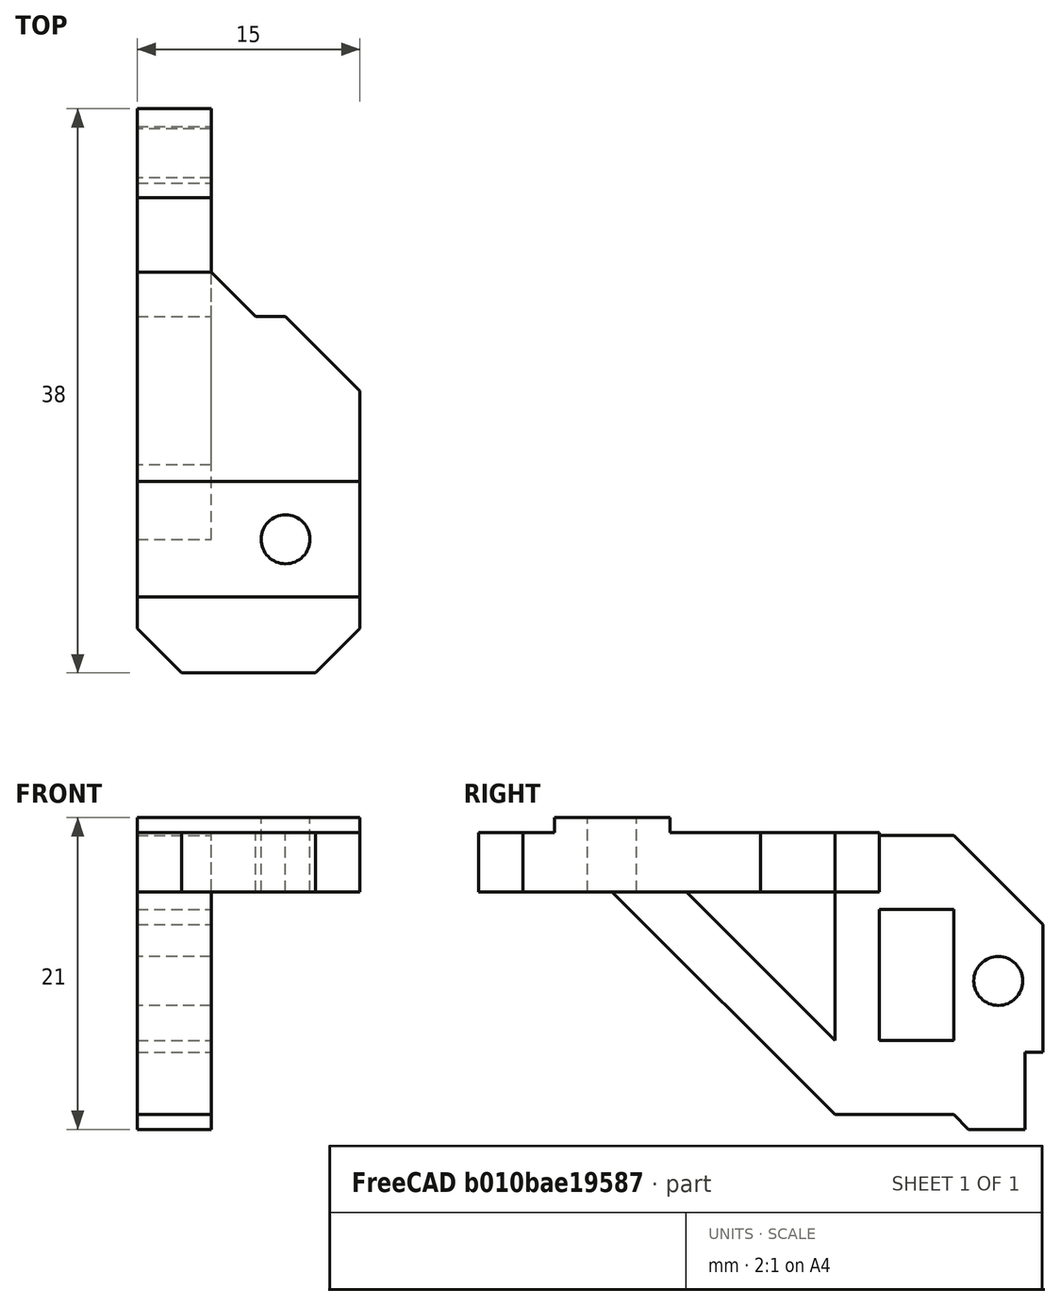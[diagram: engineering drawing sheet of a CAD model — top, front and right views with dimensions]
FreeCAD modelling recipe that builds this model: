
FCSTD DOCUMENT  (FreeCAD 0.19R24291 (Git))
Label: LCD-mount
License: Other
LicenseURL: GPL3
objects: Part::Chamfer×5, Part::Box×3, Part::Feature×1, Part::Cylinder×1, Part::MultiFuse×1, Part::Cut×1
note: 12 computed .brp shape members not serialized (recipe doc carries the construction recipe); baked Part::Feature solids carry a one-line shape summary decoded from their .brp

FEATURE [Part::Feature] Cut004005004003002008001015003001001001
  shape: bbox 5 x 14 x 20 mm, 18 faces (baked)
FEATURE [Part::Box] Box  label="Cube"
  AttacherType = Attacher::AttachEngine3D
  Height = 4
  Length = 15
  Placement = pos=(-5,-29,20) rot=(0,0,1;0rad)
  Width = 24
FEATURE [Part::Box] Box001  label="Cube001"
  AttacherType = Attacher::AttachEngine3D
  Height = 16
  Length = 5
  Placement = pos=(-5,-20,5) rot=(0,0,1;0rad)
  Width = 16
FEATURE [Part::Chamfer] Chamfer
  Base = -> Box001
  Edges = 1 edges r=15: [Edge9]
FEATURE [Part::Chamfer] Chamfer001
  Base = -> Chamfer
  Edges = 1 edges r=12: [Edge11]
FEATURE [Part::Box] Box002  label="Cube002"
  AttacherType = Attacher::AttachEngine3D
  Height = 1
  Length = 15
  Placement = pos=(-5,-23.9,24) rot=(0,0,1;0rad)
  Width = 7.8
FEATURE [Part::Chamfer] Chamfer002
  Base = -> Box
  Edges = 2 edges r=3: [Edge1,Edge5]
FEATURE [Part::Chamfer] Chamfer003
  Base = -> Chamfer002
  Edges = 1 edges r=5: [Edge13]
FEATURE [Part::Cylinder] Cylinder
  Angle = 360
  AttacherType = Attacher::AttachEngine3D
  Height = 10
  Placement = pos=(5,-20,16) rot=(0,0,1;0rad)
  Radius = 1.65
FEATURE [Part::MultiFuse] Fusion
  Shapes = -> [Chamfer003,Box002,Chamfer001,Cut004005004003002008001015003001001001]
FEATURE [Part::Cut] Cut
  Base = -> Fusion
  Tool = -> Cylinder
FEATURE [Part::Chamfer] Chamfer004
  Base = -> Cut
  Edges = 1 edges r=2.99: [Edge66]
